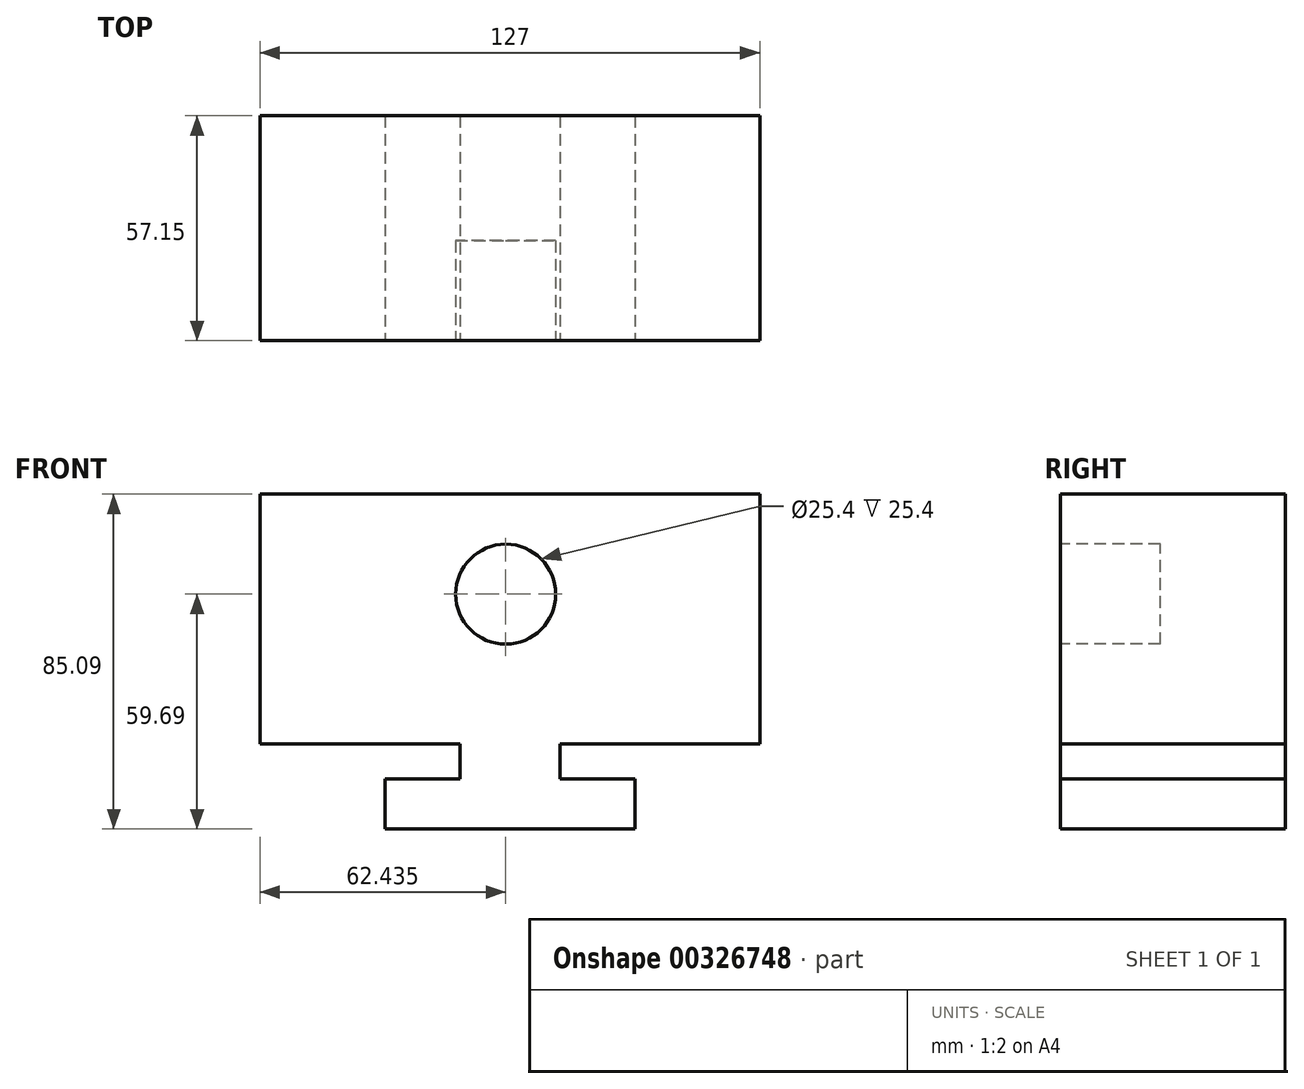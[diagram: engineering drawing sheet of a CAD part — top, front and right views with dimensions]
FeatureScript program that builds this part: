
annotation { "Feature Type Name" : "Feature", "Feature Type Description" : "" }
export const myFeature = defineFeature(function(context is Context, id is Id, definition is map)
    precondition{}
    {
        {
            var Q0;
            Q0=qCreatedBy(makeId("Front.planeOp"),FACE);
            var sketch = newSketch(context, id + "F0", { "sketchPlane" : qUnion([Q0])});
            skLineSegment(sketch, "E0.bottom", {"start": v(0, 0) * mm, "end": v(127, 0) * mm});
            skLineSegment(sketch, "E0.top", {"start": v(0, -85.1) * mm, "end": v(127, -85.1) * mm});
            skLineSegment(sketch, "E0.left", {"start": v(0, 0) * mm, "end": v(0, -85.1) * mm});
            skLineSegment(sketch, "E0.right", {"start": v(127, 0) * mm, "end": v(127, -85.1) * mm});
            skSolve(sketch);
        }
        {
            var Q0;
            Q0=makeQuery(id+"F0.imprint","IMPRINT",FACE,{"disambiguationData":[TD([[makeQuery(id+"F0.imprint","IMPRINT",EDGE,{"derivedFrom":sQuery(id+"F0.wireOp",EDGE,"E0.bottom")}),-1.0]])]});
            extrude(context, id + "F1", {"entities" : qUnion([Q0]), "depth" : 57.15 * mm});
        }
        {
            var Q0;
            Q0=makeQuery(id+"F1.opExtrude","CAP_FACE",FACE,{"disambiguationData":[OSD([sQuery(id+"F0.wireOp",EDGE,"E0.bottom"),sQuery(id+"F0.wireOp",EDGE,"E0.top"),sQuery(id+"F0.wireOp",EDGE,"E0.left"),sQuery(id+"F0.wireOp",EDGE,"E0.right")])],"isStart":false});
            var sketch = newSketch(context, id + "F2", { "sketchPlane" : qUnion([Q0])});
            skLineSegment(sketch, "E1.bottom", {"start": v(127, -85.1) * mm, "end": v(95.25, -85.1) * mm});
            skLineSegment(sketch, "E1.top", {"start": v(127, -72.39) * mm, "end": v(95.25, -72.39) * mm});
            skLineSegment(sketch, "E1.left", {"start": v(127, -85.1) * mm, "end": v(127, -72.39) * mm});
            skLineSegment(sketch, "E1.right", {"start": v(95.25, -85.1) * mm, "end": v(95.25, -72.39) * mm});
            skSolve(sketch);
        }
        {
            var Q0;
            Q0 = qSketchRegion(id + "F2", true);
            extrude(context, id + "F3", {"entities" : qUnion([Q0]), "operationType" : NewBodyOperationType.REMOVE, "oppositeDirection" : true, "depth" : 57.15 * mm});
        }
        {
            var Q0;
            Q0=makeQuery(id+"F1.opExtrude","CAP_FACE",FACE,{"disambiguationData":[OSD([sQuery(id+"F0.wireOp",EDGE,"E0.bottom"),sQuery(id+"F0.wireOp",EDGE,"E0.top"),sQuery(id+"F0.wireOp",EDGE,"E0.left"),sQuery(id+"F0.wireOp",EDGE,"E0.right")])],"isStart":false});
            var sketch = newSketch(context, id + "F4", { "sketchPlane" : qUnion([Q0])});
            skLineSegment(sketch, "E2.bottom", {"start": v(127, -72.39) * mm, "end": v(76.2, -72.39) * mm});
            skLineSegment(sketch, "E2.top", {"start": v(127, -63.5) * mm, "end": v(76.2, -63.5) * mm});
            skLineSegment(sketch, "E2.left", {"start": v(127, -72.39) * mm, "end": v(127, -63.5) * mm});
            skLineSegment(sketch, "E2.right", {"start": v(76.2, -72.39) * mm, "end": v(76.2, -63.5) * mm});
            skSolve(sketch);
        }
        {
            var Q0;
            Q0 = qSketchRegion(id + "F4", true);
            extrude(context, id + "F5", {"entities" : qUnion([Q0]), "operationType" : NewBodyOperationType.REMOVE, "oppositeDirection" : true, "depth" : 57.15 * mm});
        }
        {
            var Q0;
            Q0=makeQuery(id+"F1.opExtrude","CAP_FACE",FACE,{"disambiguationData":[OSD([sQuery(id+"F0.wireOp",EDGE,"E0.bottom"),sQuery(id+"F0.wireOp",EDGE,"E0.top"),sQuery(id+"F0.wireOp",EDGE,"E0.left"),sQuery(id+"F0.wireOp",EDGE,"E0.right")])],"isStart":false});
            var sketch = newSketch(context, id + "F6", { "sketchPlane" : qUnion([Q0])});
            skLineSegment(sketch, "E3.bottom", {"start": v(0, -85.1) * mm, "end": v(31.75, -85.1) * mm});
            skLineSegment(sketch, "E3.top", {"start": v(0, -72.4) * mm, "end": v(31.75, -72.4) * mm});
            skLineSegment(sketch, "E3.left", {"start": v(0, -85.1) * mm, "end": v(0, -72.4) * mm});
            skLineSegment(sketch, "E3.right", {"start": v(31.75, -85.1) * mm, "end": v(31.75, -72.4) * mm});
            skSolve(sketch);
        }
        {
            var Q0;
            Q0 = qSketchRegion(id + "F6", true);
            extrude(context, id + "F7", {"entities" : qUnion([Q0]), "operationType" : NewBodyOperationType.REMOVE, "oppositeDirection" : true, "depth" : 57.15 * mm});
        }
        {
            var Q0;
            Q0=makeQuery(id+"F1.opExtrude","CAP_FACE",FACE,{"disambiguationData":[OSD([sQuery(id+"F0.wireOp",EDGE,"E0.bottom"),sQuery(id+"F0.wireOp",EDGE,"E0.top"),sQuery(id+"F0.wireOp",EDGE,"E0.left"),sQuery(id+"F0.wireOp",EDGE,"E0.right")])],"isStart":false});
            var sketch = newSketch(context, id + "F8", { "sketchPlane" : qUnion([Q0])});
            skLineSegment(sketch, "E4.bottom", {"start": v(0, -72.4) * mm, "end": v(50.8, -72.4) * mm});
            skLineSegment(sketch, "E4.top", {"start": v(0, -63.5) * mm, "end": v(50.8, -63.5) * mm});
            skLineSegment(sketch, "E4.left", {"start": v(0, -72.4) * mm, "end": v(0, -63.5) * mm});
            skLineSegment(sketch, "E4.right", {"start": v(50.8, -72.4) * mm, "end": v(50.8, -63.5) * mm});
            skSolve(sketch);
        }
        {
            var Q0;
            Q0 = qSketchRegion(id + "F8", true);
            extrude(context, id + "F9", {"entities" : qUnion([Q0]), "operationType" : NewBodyOperationType.REMOVE, "oppositeDirection" : true, "depth" : 57.15 * mm});
        }
        {
            var Q0;
            Q0=makeQuery(id+"F1.opExtrude","CAP_FACE",FACE,{"disambiguationData":[OSD([sQuery(id+"F0.wireOp",EDGE,"E0.bottom"),sQuery(id+"F0.wireOp",EDGE,"E0.top"),sQuery(id+"F0.wireOp",EDGE,"E0.left"),sQuery(id+"F0.wireOp",EDGE,"E0.right")])],"isStart":false});
            var sketch = newSketch(context, id + "F10", { "sketchPlane" : qUnion([Q0])});
            skCircle(sketch, "E5", {"center": v(62.44, -25.4) * mm, "radius": 12.7 * mm});
            skSolve(sketch);
        }
        {
            var Q0;
            Q0 = qSketchRegion(id + "F10", true);
            extrude(context, id + "F11", {"entities" : qUnion([Q0]), "operationType" : NewBodyOperationType.REMOVE, "oppositeDirection" : true, "depth" : 25.4 * mm});
        }
    });
